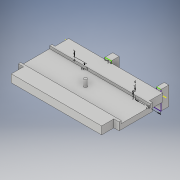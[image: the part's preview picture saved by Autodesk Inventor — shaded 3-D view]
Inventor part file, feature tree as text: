
AUTODESK INVENTOR PART (.ipt)
format: ipt  version: 2019 (Build 230136000, 136)  size: 359,936 bytes
history: native  units: mm
features: extrude x9, sketch x3
ambient origin geometry x8: Origin, YZ Plane, XZ Plane, XY Plane, X Axis, Y Axis, Z Axis, Center Point
bodies: Body1 (feature_tree)
feature tree (12):
  sketch  "Sketch1"  dims[d133=2.5mm d134=6.0mm d135=0.0mm]
  extrude  "Extrusion39"  Depth=6.0mm TaperAngle=0.0deg
  extrude  "Extrusion40"  Depth=6.0mm TaperAngle=0.0deg
  extrude  "Extrusion41"  Depth=78.0mm
  extrude  "Extrusion42"  Depth=22.5mm
  extrude  "Extrusion43"  Depth=2.0mm TaperAngle=0.0deg
  sketch  "Sketch31"  dims[d140=9.0mm d141=0.0mm d142=78.0mm d143=22.5mm d144=2.0mm d145=0.0mm d152=5.0mm d157=20.0mm d163=4.0mm d164=4.0mm d169=36.0mm d170=4.0mm d171=5.0mm d180=46.0mm d181=10.0mm d182=0.0mm d183=10.0mm d184=0.0mm d187=3.0mm d188=3.0mm d189=6.0mm d190=0.0mm d191=6.0mm d192=0.0mm]
  extrude  "Extrusion51"  Depth=5.0mm
  extrude  "Extrusion52"  Depth=20.0mm
  extrude  "Extrusion54"  Depth=4.0mm
  extrude  "Extrusion55"  Depth=4.0mm
  sketch  "Sketch30"  dims[d136=2.0mm d137=0.0mm d138=6.0mm d139=0.0mm]
